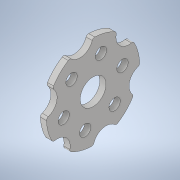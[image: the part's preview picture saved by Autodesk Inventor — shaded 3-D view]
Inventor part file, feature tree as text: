
AUTODESK INVENTOR PART (.ipt)
format: ipt  version: 2021 (Build 250183000, 183)  size: 173,568 bytes
history: native  units: in
note: dims shown in document units (in); Inventor stores cm internally (conversion verified against a paired STEP export)
features: extrude x1, fillet x1, sketch x1
ambient origin geometry x8: Origin, YZ Plane, XZ Plane, XY Plane, X Axis, Y Axis, Z Axis, Center Point
bodies: Solid1 (feature_tree)
feature tree (3):
  extrude  "Extrusion1"  Depth=0.125in
  fillet  "Fillet1"  Radius=0.55in
  sketch  "Sketch1"  dims[d0=4.517in d1=2.952in d2=0.55in d3=45.0deg d4=2.3622in d6=360.0deg d8=1.25in d12=1.25in d16=15.0deg d17=2.3622in d19=360.0deg d21=0.296in d22=0.0in d23=0.125in]
